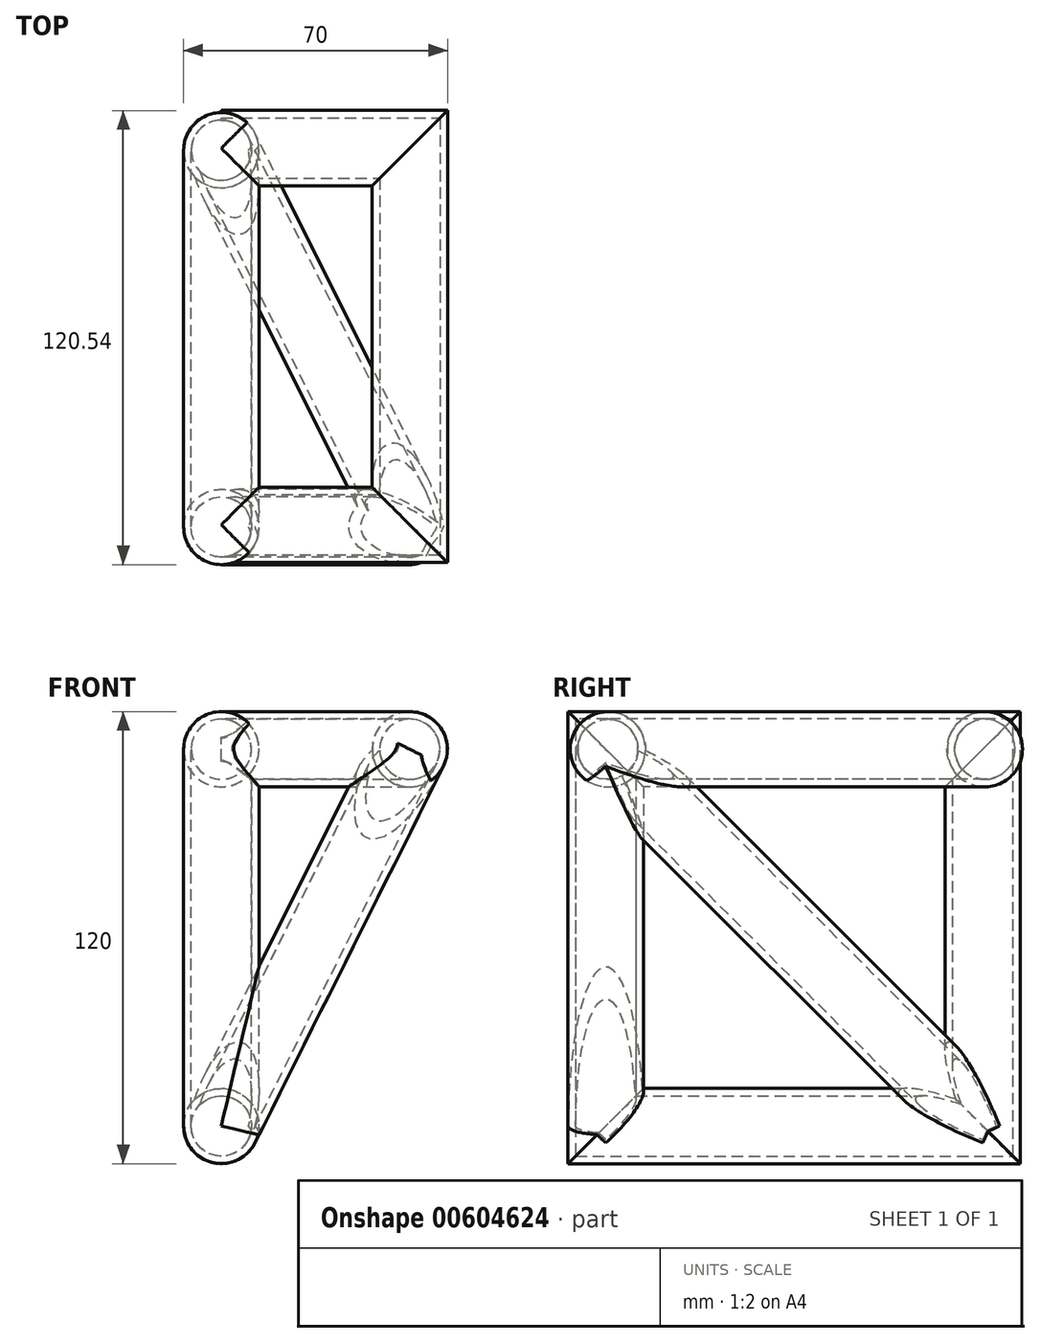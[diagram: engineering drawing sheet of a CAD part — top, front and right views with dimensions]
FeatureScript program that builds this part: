
annotation { "Feature Type Name" : "Feature", "Feature Type Description" : "" }
export const myFeature = defineFeature(function(context is Context, id is Id, definition is map)
    precondition{}
    {
        {
            var Q0;
            Q0=qCreatedBy(makeId("Right.planeOp"),FACE);
            var sketch = newSketch(context, id + "F0", { "sketchPlane" : qUnion([Q0])});
            skLineSegment(sketch, "E0.bottom", {"start": v(-50, 50) * mm, "end": v(50, 50) * mm});
            skLineSegment(sketch, "E0.top", {"start": v(-50, -50) * mm, "end": v(50, -50) * mm});
            skLineSegment(sketch, "E0.left", {"start": v(-50, 50) * mm, "end": v(-50, -50) * mm});
            skLineSegment(sketch, "E0.right", {"start": v(50, 50) * mm, "end": v(50, -50) * mm});
            skSolve(sketch);
        }
        {
            var Q0;
            Q0=qCreatedBy(makeId("Front.planeOp"),FACE);
            var sketch = newSketch(context, id + "F1", { "sketchPlane" : qUnion([Q0])});
            skCircle(sketch, "E1", {"center": v(0, 50) * mm, "radius": 10 * mm});
            skCircle(sketch, "E2", {"center": v(0, 50) * mm, "radius": 8 * mm});
            skSolve(sketch);
        }
        {
            var Q0;
            Q0=makeQuery(id+"F1.imprint","IMPRINT",FACE,{"disambiguationData":[TD([[makeQuery(id+"F1.imprint","IMPRINT",EDGE,{"derivedFrom":sQuery(id+"F1.wireOp",EDGE,"E1")}),1.0]])]});
            var Q1;
            Q1 = qConstructionFilter(qBodyType(qCreatedBy(id + "F0" ,EDGE), BodyType.WIRE), ConstructionObject.NO);
            sweep(context, id + "F2", {"profiles" : qUnion([Q0]), "path" : qUnion([Q1])});
        }
        {
            var Q0;
            Q0=qCreatedBy(makeId("Front.planeOp"),FACE);
            var sketch = newSketch(context, id + "F3", { "sketchPlane" : qUnion([Q0])});
            skLineSegment(sketch, "E3.bottom", {"start": v(0, 66.88) * mm, "end": v(20.98, 66.88) * mm});
            skLineSegment(sketch, "E3.top", {"start": v(0, -65.78) * mm, "end": v(20.98, -65.78) * mm});
            skLineSegment(sketch, "E3.left", {"start": v(0, 66.88) * mm, "end": v(0, -65.78) * mm});
            skLineSegment(sketch, "E3.right", {"start": v(20.98, 66.88) * mm, "end": v(20.98, -65.78) * mm});
            skSolve(sketch);
        }
        {
            var Q0;
            Q0=qCreatedBy(makeId("Top.planeOp"),FACE);
            cPlane(context, id + "F4", {"entities" : qUnion([Q0]), "cplaneType" : CPlaneType.OFFSET, "offset" : 50 * mm, "width" : 150 * mm, "height" : 150 * mm});
        }
        {
            var Q0;
            Q0=qCreatedBy(id+"F4.planeOp",FACE);
            var sketch = newSketch(context, id + "F5", { "sketchPlane" : qUnion([Q0])});
            skLineSegment(sketch, "E4.bottom", {"start": v(0, 50.54) * mm, "end": v(50, 50.54) * mm});
            skLineSegment(sketch, "E4.top", {"start": v(0, -49.46) * mm, "end": v(50, -49.46) * mm});
            skLineSegment(sketch, "E4.right", {"start": v(50, 50.54) * mm, "end": v(50, -49.46) * mm});
            skSolve(sketch);
        }
        {
            var Q0;
            Q0=qCreatedBy(makeId("Front.planeOp"),FACE);
            var sketch = newSketch(context, id + "F6", { "sketchPlane" : qUnion([Q0])});
            skCircle(sketch, "E5", {"center": v(50, 50) * mm, "radius": 10 * mm});
            skCircle(sketch, "E6", {"center": v(50, 50) * mm, "radius": 8 * mm});
            skSolve(sketch);
        }
        {
            var Q0;
            Q0=makeQuery(id+"F6.imprint","IMPRINT",FACE,{"disambiguationData":[TD([[makeQuery(id+"F6.imprint","IMPRINT",EDGE,{"derivedFrom":sQuery(id+"F6.wireOp",EDGE,"E5")}),1.0]])]});
            var Q1;
            Q1 = qConstructionFilter(qBodyType(qCreatedBy(id + "F5" ,EDGE), BodyType.WIRE), ConstructionObject.NO);
            sweep(context, id + "F7", {"operationType" : NewBodyOperationType.ADD, "profiles" : qUnion([Q0]), "path" : qUnion([Q1])});
        }
        {
            var Q0;
            Q0=qCreatedBy(makeId("Front.planeOp"),FACE);
            cPlane(context, id + "F8", {"entities" : qUnion([Q0]), "cplaneType" : CPlaneType.OFFSET, "offset" : 50 * mm, "width" : 150 * mm, "height" : 150 * mm});
        }
        {
            var Q0;
            Q0=qCreatedBy(id+"F8.planeOp",FACE);
            var sketch = newSketch(context, id + "F9", { "sketchPlane" : qUnion([Q0])});
            skLineSegment(sketch, "E7", {"start": v(0, -50) * mm, "end": v(50, 50) * mm});
            skSolve(sketch);
        }
        {
            var Q0;
            Q0=sQuery(id+"F9.wireOp",EDGE,"E7");
            var Q1;
            Q1=sQuery(id+"F9.wireOp",VERTEX,"E7.end");
            cPlane(context, id + "F10", {"entities" : qUnion([Q0, Q1]), "cplaneType" : CPlaneType.LINE_POINT, "offset" : 25 * mm, "oppositeDirection" : true, "width" : 150 * mm, "height" : 150 * mm});
        }
        {
            var Q0;
            Q0=qCreatedBy(id+"F10.planeOp",FACE);
            var sketch = newSketch(context, id + "F11", { "sketchPlane" : qUnion([Q0])});
            skCircle(sketch, "E8", {"center": v(22.36, -50) * mm, "radius": 10 * mm});
            skCircle(sketch, "E9", {"center": v(22.36, -50) * mm, "radius": 8 * mm});
            skSolve(sketch);
        }
        {
            var Q0;
            Q0 = qSketchRegion(id + "F11", true);
            var Q1;
            Q1 = qConstructionFilter(qBodyType(qCreatedBy(id + "F11" ,EDGE), BodyType.WIRE), ConstructionObject.NO);
            var Q2;
            Q2=sQuery(id+"F9.wireOp",EDGE,"E7");
            sweep(context, id + "F12", {"operationType" : NewBodyOperationType.ADD, "profiles" : qUnion([Q0]), "surfaceProfiles" : qUnion([Q1]), "path" : qUnion([Q2])});
        }
        {
            var Q0;
            Q0=qCreatedBy(makeId("Top.planeOp"),FACE);
            var sketch = newSketch(context, id + "F13", { "sketchPlane" : qUnion([Q0])});
            skLineSegment(sketch, "E10.bottom", {"start": v(-66.67, -50.67) * mm, "end": v(94.29, -50.67) * mm});
            skLineSegment(sketch, "E10.top", {"start": v(-66.67, -93.85) * mm, "end": v(94.29, -93.85) * mm});
            skLineSegment(sketch, "E10.left", {"start": v(-66.67, -50.67) * mm, "end": v(-66.67, -93.85) * mm});
            skLineSegment(sketch, "E10.right", {"start": v(94.29, -50.67) * mm, "end": v(94.29, -93.85) * mm});
            skSolve(sketch);
        }
        {
            var Q0;
            Q0=qCreatedBy(id+"F10.planeOp",FACE);
            var sketch = newSketch(context, id + "F14", { "sketchPlane" : qUnion([Q0])});
            skCircle(sketch, "E11", {"center": v(22.36, -50) * mm, "radius": 8 * mm});
            skSolve(sketch);
        }
        {
            var Q0;
            Q0=qCreatedBy(makeId("Front.planeOp"),FACE);
            var sketch = newSketch(context, id + "F15", { "sketchPlane" : qUnion([Q0])});
            skCircle(sketch, "E12", {"center": v(50, 50) * mm, "radius": 8 * mm});
            skSolve(sketch);
        }
        {
            var Q0;
            Q0=qCreatedBy(makeId("Front.planeOp"),FACE);
            var sketch = newSketch(context, id + "F16", { "sketchPlane" : qUnion([Q0])});
            skCircle(sketch, "E13", {"center": v(0, 50) * mm, "radius": 8 * mm});
            skSolve(sketch);
        }
        {
            var Q0;
            Q0=qCreatedBy(makeId("Right.planeOp"),FACE);
            var sketch = newSketch(context, id + "F17", { "sketchPlane" : qUnion([Q0])});
            skCircle(sketch, "E14", {"center": v(50, -50) * mm, "radius": 8.85 * mm, "construction": true});
            skSolve(sketch);
        }
        {
            var Q0;
            Q0=sQuery(id+"F9.wireOp",VERTEX,"E7.end");
            var Q1;
            Q1=sQuery(id+"F9.wireOp",VERTEX,"E7.start");
            var Q2;
            Q2=sQuery(id+"F17.wireOp",VERTEX,"E14.center");
            cPlane(context, id + "F18", {"entities" : qUnion([Q0, Q1, Q2]), "cplaneType" : CPlaneType.THREE_POINT, "offset" : 25 * mm, "width" : 150 * mm, "height" : 150 * mm});
        }
        {
            var Q0;
            Q0=qCreatedBy(id+"F18.planeOp",FACE);
            var sketch = newSketch(context, id + "F19", { "sketchPlane" : qUnion([Q0])});
            skLineSegment(sketch, "E15", {"start": v(-50, -44.72) * mm, "end": v(50, 67.08) * mm});
            skSolve(sketch);
        }
        {
            var Q0;
            Q0=sQuery(id+"F19.wireOp",VERTEX,"E15.end");
            var Q1;
            Q1=sQuery(id+"F19.wireOp",EDGE,"E15");
            cPlane(context, id + "F20", {"entities" : qUnion([Q0, Q1]), "cplaneType" : CPlaneType.LINE_POINT, "offset" : 25 * mm, "width" : 150 * mm, "height" : 150 * mm});
        }
        {
            var Q0;
            Q0=qCreatedBy(id+"F20.planeOp",FACE);
            var sketch = newSketch(context, id + "F21", { "sketchPlane" : qUnion([Q0])});
            skCircle(sketch, "E16", {"center": v(23.57, 0) * mm, "radius": 8 * mm});
            skCircle(sketch, "E17", {"center": v(23.57, 0) * mm, "radius": 10 * mm});
            skSolve(sketch);
        }
        {
            var Q0;
            Q0=makeQuery(id+"F21.imprint","IMPRINT",FACE,{"disambiguationData":[TD([[makeQuery(id+"F21.imprint","IMPRINT",EDGE,{"derivedFrom":sQuery(id+"F21.wireOp",EDGE,"E16")}),-1.0]])]});
            var sketch = newSketch(context, id + "F22", { "sketchPlane" : qUnion([Q0])});
            skCircle(sketch, "E18", {"center": v(23.57, 0) * mm, "radius": 8 * mm});
            skSolve(sketch);
        }
        {
            var Q0;
            Q0 = qSketchRegion(id + "F21", true);
            var Q1;
            Q1=sQuery(id+"F19.wireOp",EDGE,"E15");
            sweep(context, id + "F23", {"operationType" : NewBodyOperationType.ADD, "profiles" : qUnion([Q0]), "path" : qUnion([Q1])});
        }
        {
            var Q0;
            Q0 = qSketchRegion(id + "F14", true);
            var Q1;
            Q1=sQuery(id+"F9.wireOp",EDGE,"E7");
            sweep(context, id + "F24", {"operationType" : NewBodyOperationType.REMOVE, "profiles" : qUnion([Q0]), "path" : qUnion([Q1])});
        }
        {
            var Q0;
            Q0 = qSketchRegion(id + "F16", true);
            var Q1;
            Q1 = qConstructionFilter(qBodyType(qCreatedBy(id + "F0" ,EDGE), BodyType.WIRE), ConstructionObject.NO);
            sweep(context, id + "F25", {"operationType" : NewBodyOperationType.REMOVE, "profiles" : qUnion([Q0]), "path" : qUnion([Q1])});
        }
        {
            var Q0;
            Q0 = qSketchRegion(id + "F15", true);
            var Q1;
            Q1 = qConstructionFilter(qBodyType(qCreatedBy(id + "F5" ,EDGE), BodyType.WIRE), ConstructionObject.NO);
            sweep(context, id + "F26", {"operationType" : NewBodyOperationType.REMOVE, "profiles" : qUnion([Q0]), "path" : qUnion([Q1])});
        }
        {
            var Q0;
            Q0 = qSketchRegion(id + "F22", true);
            var Q1;
            Q1 = qConstructionFilter(qBodyType(qCreatedBy(id + "F19" ,EDGE), BodyType.WIRE), ConstructionObject.NO);
            sweep(context, id + "F27", {"operationType" : NewBodyOperationType.REMOVE, "profiles" : qUnion([Q0]), "path" : qUnion([Q1])});
        }
    });
